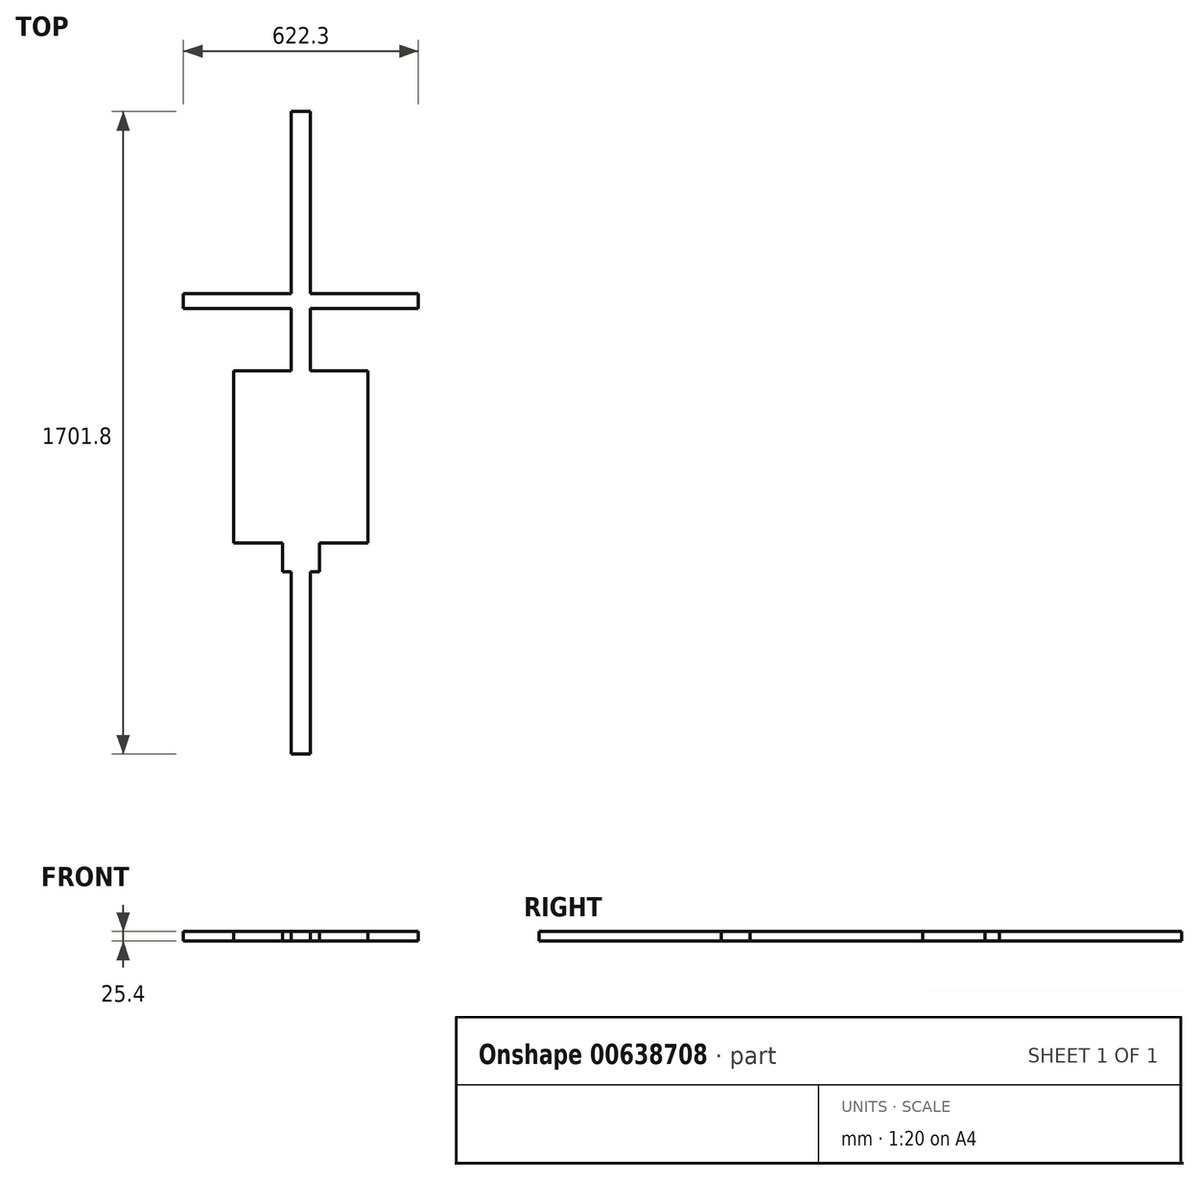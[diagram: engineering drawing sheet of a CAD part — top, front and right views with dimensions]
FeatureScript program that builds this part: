
annotation { "Feature Type Name" : "Feature", "Feature Type Description" : "" }
export const myFeature = defineFeature(function(context is Context, id is Id, definition is map)
    precondition{}
    {
        {
            var Q0;
            Q0=qCreatedBy(makeId("Top.planeOp"),FACE);
            var sketch = newSketch(context, id + "F0", { "sketchPlane" : qUnion([Q0])});
            skLineSegment(sketch, "E0.bottom", {"start": v(-25.4, 0) * mm, "end": v(25.4, 0) * mm});
            skLineSegment(sketch, "E0.top", {"start": v(-25.4, 1701.8) * mm, "end": v(25.4, 1701.8) * mm});
            skLineSegment(sketch, "E0.left", {"start": v(-25.4, 0) * mm, "end": v(-25.4, 1701.8) * mm});
            skLineSegment(sketch, "E0.right", {"start": v(25.4, 0) * mm, "end": v(25.4, 1701.8) * mm});
            skLineSegment(sketch, "E1.bottom", {"start": v(48.57, 482.6) * mm, "end": v(-48.57, 482.6) * mm});
            skLineSegment(sketch, "E1.top", {"start": v(48.57, 704.32) * mm, "end": v(-48.57, 704.32) * mm});
            skLineSegment(sketch, "E1.left", {"start": v(48.57, 482.6) * mm, "end": v(48.57, 704.32) * mm});
            skLineSegment(sketch, "E1.right", {"start": v(-48.57, 482.6) * mm, "end": v(-48.57, 704.32) * mm});
            skPoint(sketch, "E1.middle", {"position": v(0, 593.46) * mm});
            skLineSegment(sketch, "E2.bottom", {"start": v(311.15, 1180.77) * mm, "end": v(-311.15, 1180.77) * mm});
            skLineSegment(sketch, "E2.top", {"start": v(311.15, 1219.2) * mm, "end": v(-311.15, 1219.2) * mm});
            skLineSegment(sketch, "E2.left", {"start": v(311.15, 1180.77) * mm, "end": v(311.15, 1219.2) * mm});
            skLineSegment(sketch, "E2.right", {"start": v(-311.15, 1180.77) * mm, "end": v(-311.15, 1219.2) * mm});
            skPoint(sketch, "E2.middle", {"position": v(0, 1199.98) * mm});
            skLineSegment(sketch, "E3.bottom", {"start": v(177.8, 558.8) * mm, "end": v(-177.8, 558.8) * mm});
            skLineSegment(sketch, "E3.top", {"start": v(177.8, 1015.55) * mm, "end": v(-177.8, 1015.55) * mm});
            skLineSegment(sketch, "E3.left", {"start": v(177.8, 558.8) * mm, "end": v(177.8, 1015.55) * mm});
            skLineSegment(sketch, "E3.right", {"start": v(-177.8, 558.8) * mm, "end": v(-177.8, 1015.55) * mm});
            skPoint(sketch, "E3.middle", {"position": v(0, 787.17) * mm});
            skSolve(sketch);
        }
        {
            var Q0;
            Q0 = qSketchRegion(id + "F0", true);
            var Q1;
            {var subQ0=sQuery(id+"F0.wireOp",EDGE,"E3.bottom");var subQ1=sQuery(id+"F0.wireOp",EDGE,"E0.left");var subQ2=makeQuery(id+"F0.imprint","INTERSECT",VERTEX,{"derivedFrom":[subQ1,subQ0]});Q1=makeQuery(id+"F0.imprint","IMPRINT",FACE,{"disambiguationData":[TD([[makeQuery(id+"F0.imprint","IMPRINT",EDGE,{"disambiguationData":[TD([[subQ2,-1.0]])],"derivedFrom":subQ1}),-1.0]])]});}
            extrude(context, id + "F1", {"entities" : qUnion([Q0, Q1]), "depth" : 25.4 * mm, "offsetDistance" : 25.4 * mm});
        }
    });
